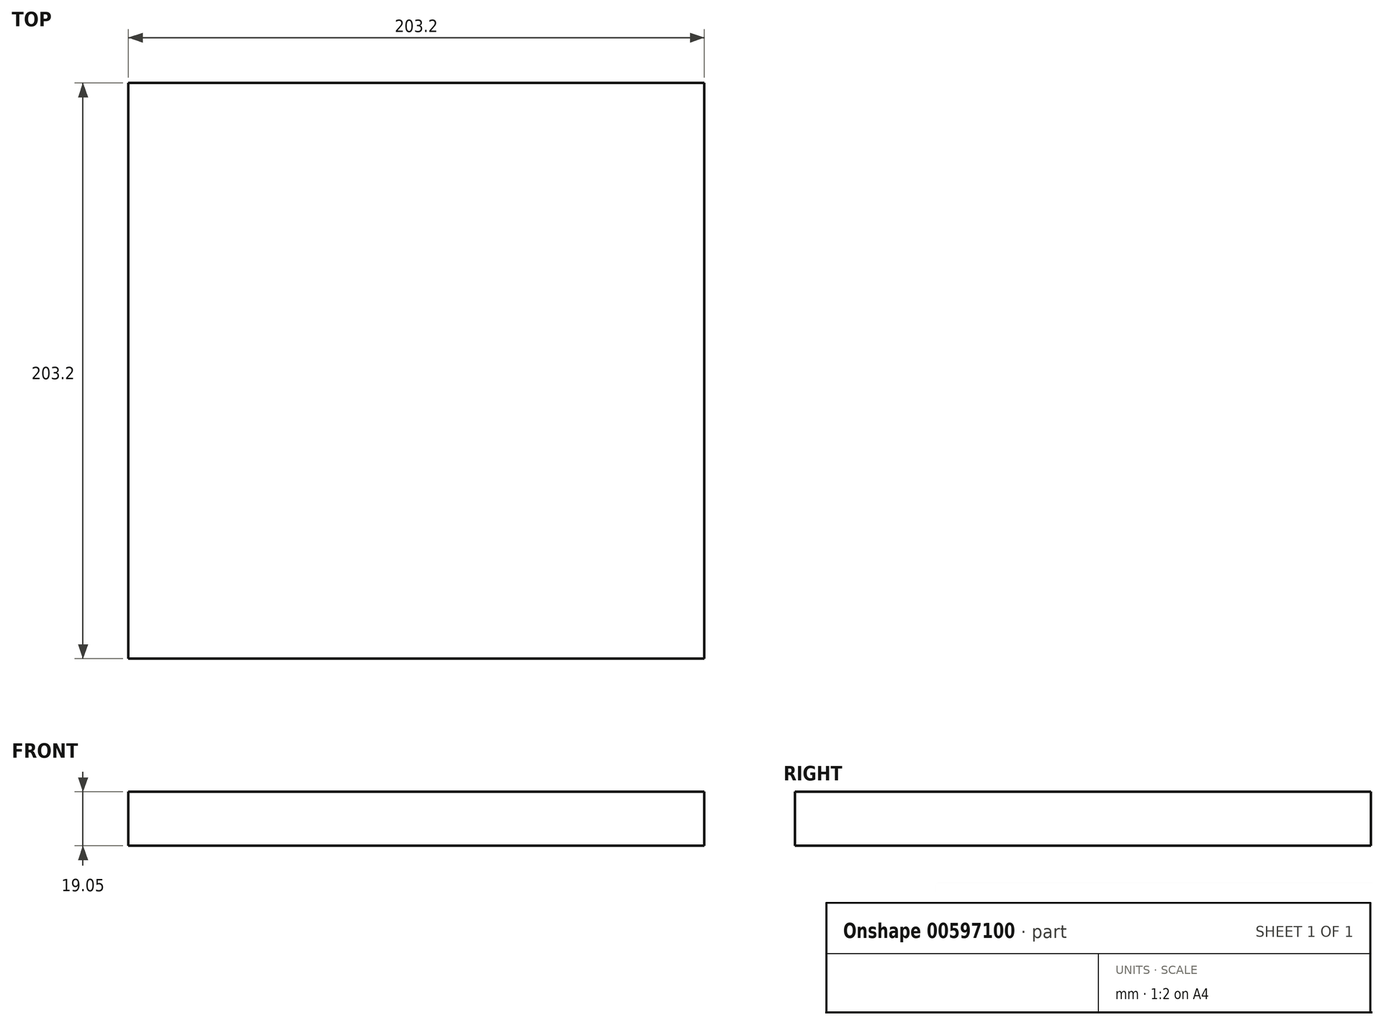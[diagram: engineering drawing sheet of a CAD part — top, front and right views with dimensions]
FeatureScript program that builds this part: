
annotation { "Feature Type Name" : "Feature", "Feature Type Description" : "" }
export const myFeature = defineFeature(function(context is Context, id is Id, definition is map)
    precondition{}
    {
        {
            var Q0;
            Q0=qCreatedBy(makeId("Top.planeOp"),FACE);
            var sketch = newSketch(context, id + "F0", { "sketchPlane" : qUnion([Q0])});
            skLineSegment(sketch, "E0.bottom", {"start": v(-138.7, 143.63) * mm, "end": v(64.5, 143.63) * mm});
            skLineSegment(sketch, "E0.top", {"start": v(-138.7, -59.57) * mm, "end": v(64.5, -59.57) * mm});
            skLineSegment(sketch, "E0.left", {"start": v(-138.7, 143.63) * mm, "end": v(-138.7, -59.57) * mm});
            skLineSegment(sketch, "E0.right", {"start": v(64.5, 143.63) * mm, "end": v(64.5, -59.57) * mm});
            skPoint(sketch, "E1.center.orphan", {"position": v(0, 137.82) * mm});
            skSolve(sketch);
        }
        {
            var Q0;
            Q0=makeQuery(id+"F0.imprint","IMPRINT",FACE,{"disambiguationData":[TD([[makeQuery(id+"F0.imprint","IMPRINT",EDGE,{"derivedFrom":sQuery(id+"F0.wireOp",EDGE,"E0.bottom")}),-1.0]])]});
            extrude(context, id + "F1", {"entities" : qUnion([Q0]), "depth" : 19.05 * mm, "offsetDistance" : 25.4 * mm});
        }
    });
